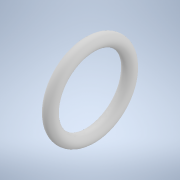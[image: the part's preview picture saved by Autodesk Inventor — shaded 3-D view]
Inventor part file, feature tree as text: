
AUTODESK INVENTOR PART (.ipt)
format: ipt  version: 2021 (Build 250183000, 183)  size: 135,168 bytes
history: native  units: mm
features: revolve x1, sketch x1
ambient origin geometry x8: Origin, YZ Plane, XZ Plane, XY Plane, X Axis, Y Axis, Z Axis, Center Point
bodies: Solid1 (feature_tree)
feature tree (2):
  revolve  "Revolution1"  [1 undecoded]
  sketch  "Sketch1"  dims[d0=5.0mm d1=16.5mm d2=90.0deg]
note: 1 required parameter value undecoded (feature->parameter linkage not recoverable at this tier; creation-order binding heuristic only, values carry confidence <= 0.55)
